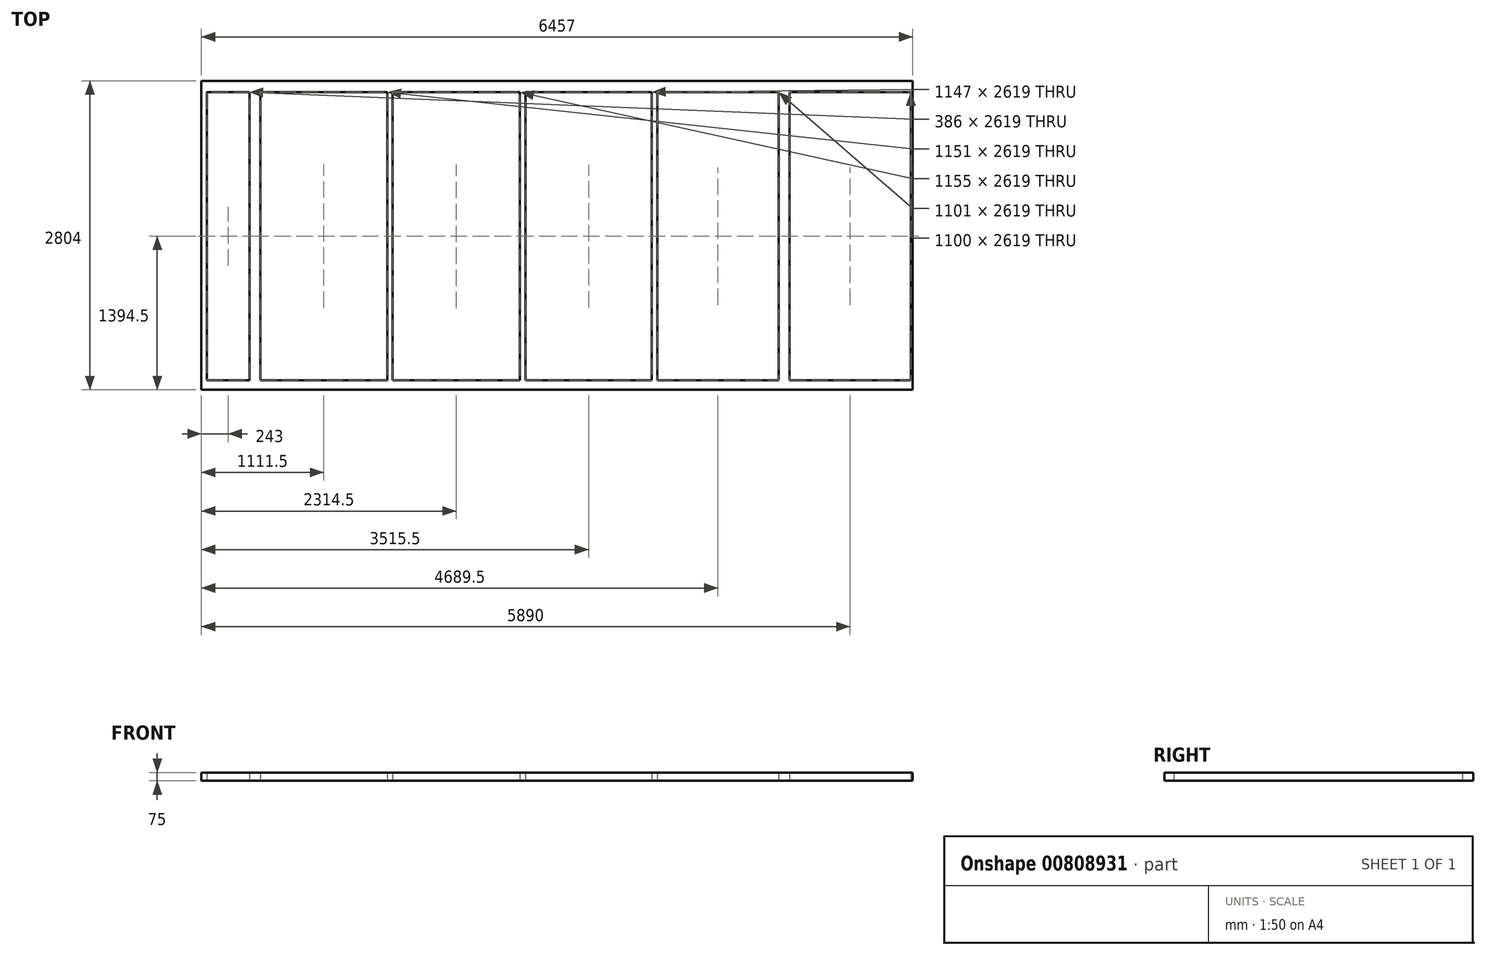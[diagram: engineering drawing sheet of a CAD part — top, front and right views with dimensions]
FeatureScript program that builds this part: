
annotation { "Feature Type Name" : "Feature", "Feature Type Description" : "" }
export const myFeature = defineFeature(function(context is Context, id is Id, definition is map)
    precondition{}
    {
        {
            var Q0;
            Q0=qCreatedBy(makeId("Top.planeOp"),FACE);
            var sketch = newSketch(context, id + "F0", { "sketchPlane" : qUnion([Q0])});
            skLineSegment(sketch, "E0.left", {"start": v(0, 0) * mm, "end": v(0, 2719) * mm});
            skLineSegment(sketch, "E0.right", {"start": v(50, 0) * mm, "end": v(50, 2619) * mm});
            skLineSegment(sketch, "E1.left", {"start": v(436, 0) * mm, "end": v(436, 2619) * mm});
            skLineSegment(sketch, "E1.right", {"start": v(536, 0) * mm, "end": v(536, 2619) * mm});
            skLineSegment(sketch, "E2.left", {"start": v(5240, 0) * mm, "end": v(5240, 2619) * mm});
            skLineSegment(sketch, "E2.right", {"start": v(5340, 0) * mm, "end": v(5340, 2619) * mm});
            skLineSegment(sketch, "E3.left", {"start": v(1687, 0) * mm, "end": v(1687, 2619) * mm});
            skLineSegment(sketch, "E3.right", {"start": v(1737, 0) * mm, "end": v(1737, 2619) * mm});
            skLineSegment(sketch, "E4.bottom", {"start": v(2892, 0) * mm, "end": v(2942, 0) * mm});
            skLineSegment(sketch, "E4.left", {"start": v(2892, 0) * mm, "end": v(2892, 2619) * mm});
            skLineSegment(sketch, "E4.right", {"start": v(2942, 0) * mm, "end": v(2942, 2619) * mm});
            skLineSegment(sketch, "E5.left", {"start": v(6457, 0) * mm, "end": v(6457, 2619) * mm});
            skLineSegment(sketch, "E5.right", {"start": v(6440, 0) * mm, "end": v(6440, 2619) * mm});
            skLineSegment(sketch, "E6.left", {"start": v(4139, 0) * mm, "end": v(4139, 2619) * mm});
            skLineSegment(sketch, "E6.right", {"start": v(4089, 0) * mm, "end": v(4089, 2619) * mm});
            skLineSegment(sketch, "E7.bottom", {"start": v(6440, 0) * mm, "end": v(5340, 0) * mm});
            skLineSegment(sketch, "E7.top", {"start": v(6457, -85) * mm, "end": v(0, -85) * mm});
            skLineSegment(sketch, "E7.left", {"start": v(6457, 0) * mm, "end": v(6457, -85) * mm});
            skLineSegment(sketch, "E7.right", {"start": v(0, 0) * mm, "end": v(0, -85) * mm});
            skLineSegment(sketch, "E8.bottom", {"start": v(6440, 2619) * mm, "end": v(5340, 2619) * mm});
            skLineSegment(sketch, "E8.top", {"start": v(6457, 2719) * mm, "end": v(50, 2719) * mm});
            skLineSegment(sketch, "E8.left", {"start": v(6457, 2619) * mm, "end": v(6457, 2719) * mm});
            skLineSegment(sketch, "E9.trimOffspring", {"start": v(5240, 2619) * mm, "end": v(4139, 2619) * mm});
            skLineSegment(sketch, "E10.trimOffspring", {"start": v(4089, 2619) * mm, "end": v(2942, 2619) * mm});
            skLineSegment(sketch, "E11.trimOffspring", {"start": v(2892, 2619) * mm, "end": v(1737, 2619) * mm});
            skLineSegment(sketch, "E12.trimOffspring", {"start": v(1687, 2619) * mm, "end": v(536, 2619) * mm});
            skLineSegment(sketch, "E13.trimOffspring", {"start": v(436, 2619) * mm, "end": v(50, 2619) * mm});
            skLineSegment(sketch, "E14.trimOffspring", {"start": v(436, 0) * mm, "end": v(50, 0) * mm});
            skLineSegment(sketch, "E15.trimOffspring", {"start": v(1687, 0) * mm, "end": v(536, 0) * mm});
            skLineSegment(sketch, "E16.trimOffspring", {"start": v(4089, 0) * mm, "end": v(1737, 0) * mm});
            skLineSegment(sketch, "E17.trimOffspring", {"start": v(5240, 0) * mm, "end": v(4139, 0) * mm});
            skLineSegment(sketch, "E18", {"start": v(50, 2719) * mm, "end": v(0, 2719) * mm});
            skSolve(sketch);
        }
        {
            var Q0;
            Q0=makeQuery(id+"F0.imprint","IMPRINT",FACE,{"disambiguationData":[TD([[makeQuery(id+"F0.imprint","IMPRINT",EDGE,{"derivedFrom":sQuery(id+"F0.wireOp",EDGE,"E0.left")}),-1.0]])]});
            extrude(context, id + "F1", {"entities" : qUnion([Q0]), "depth" : 75 * mm, "offsetDistance" : 25 * mm});
        }
    });
